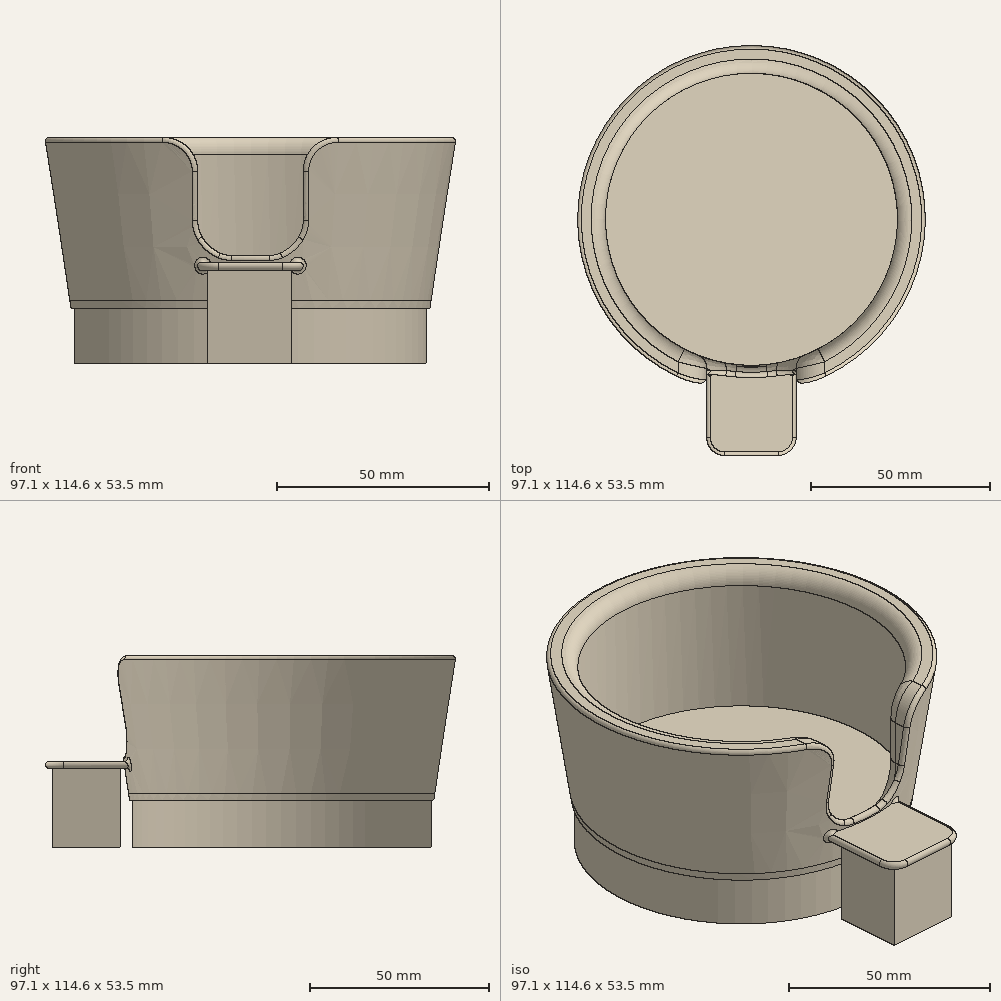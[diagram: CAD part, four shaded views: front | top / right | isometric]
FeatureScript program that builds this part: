
annotation { "Feature Type Name" : "Feature", "Feature Type Description" : "" }
export const myFeature = defineFeature(function(context is Context, id is Id, definition is map)
    precondition{}
    {
        {
            var Q0;
            Q0=qCreatedBy(makeId("Top.planeOp"),FACE);
            var sketch = newSketch(context, id + "F0", { "sketchPlane" : qUnion([Q0])});
            skCircle(sketch, "E0", {"center": v(0, 0) * mm, "radius": 34.5 * mm});
            skSolve(sketch);
        }
        {
            var Q0;
            Q0=qSketchRegion(id+"F0",true);
            extrude(context, id + "F1", {"entities" : qUnion([Q0]), "depth" : 13 * mm, "offsetDistance" : 25 * mm, "hasDraft" : true, "draftAngle" : 8.75 * degree});
        }
        {
            var Q0;
            Q0=makeQuery(id+"F1.opExtrude","CAP_FACE",FACE,{"disambiguationData":[OSD([sQuery(id+"F0.wireOp",EDGE,"E0")])],"isStart":false});
            var sketch = newSketch(context, id + "F2", { "sketchPlane" : qUnion([Q0])});
            skCircle(sketch, "E1", {"center": v(0, 0) * mm, "radius": 42.5 * mm});
            skSolve(sketch);
        }
        {
            var Q0;
            Q0=qSketchRegion(id+"F2",true);
            extrude(context, id + "F3", {"entities" : qUnion([Q0]), "operationType" : NewBodyOperationType.ADD, "depth" : 2 * mm, "offsetDistance" : 25 * mm, "hasDraft" : true, "draftAngle" : 8.7 * degree});
        }
        {
            var Q0;
            Q0=qCreatedBy(makeId("Right.planeOp"),FACE);
            var sketch = newSketch(context, id + "F4", { "sketchPlane" : qUnion([Q0])});
            skPoint(sketch, "E2", {"position": v(0, 15) * mm});
            skPoint(sketch, "E3", {"position": v(-42.8, 15) * mm});
            skPoint(sketch, "E4", {"position": v(-40.8, 15) * mm});
            skLineSegment(sketch, "E5", {"start": v(-42.8, 15) * mm, "end": v(-48.74, 53.55) * mm});
            skLineSegment(sketch, "E6", {"start": v(-42.8, 15) * mm, "end": v(-42.8, 65.75) * mm, "construction": true});
            skLineSegment(sketch, "E7", {"start": v(0, 15) * mm, "end": v(0, 72.45) * mm, "construction": true});
            skLineSegment(sketch, "E8", {"start": v(-40.8, 15) * mm, "end": v(-42.8, 15) * mm});
            skLineSegment(sketch, "E9", {"start": v(-46.74, 53.55) * mm, "end": v(-48.74, 53.55) * mm, "construction": true});
            skLineSegment(sketch, "E10", {"start": v(-40.8, 15) * mm, "end": v(-40.8, 53.55) * mm});
            skLineSegment(sketch, "E11", {"start": v(-48.74, 53.55) * mm, "end": v(-40.8, 53.55) * mm});
            skSolve(sketch);
        }
        {
            var Q0;
            Q0=qSketchRegion(id+"F4",true);
            var Q1;
            Q1=sQuery(id+"F4.wireOp",EDGE,"E7");
            revolve(context, id + "F5", {"operationType" : NewBodyOperationType.ADD, "surfaceOperationType" : NewSurfaceOperationType.NEW, "entities" : qUnion([Q0]), "axis" : qUnion([Q1]), "revolveType" : RevolveType.FULL});
        }
        {
            var Q0;
            Q0=qCreatedBy(makeId("Front.planeOp"),FACE);
            var sketch = newSketch(context, id + "F6", { "sketchPlane" : qUnion([Q0])});
            skPoint(sketch, "E12", {"position": v(0, 13) * mm});
            skPoint(sketch, "E13", {"position": v(0, 26) * mm});
            skPoint(sketch, "E14", {"position": v(0, 66) * mm});
            skPoint(sketch, "E15", {"position": v(-12.5, 66) * mm});
            skPoint(sketch, "E16", {"position": v(12.5, 66) * mm});
            skLineSegment(sketch, "E17.bottom", {"start": v(-12.5, 66) * mm, "end": v(12.5, 66) * mm});
            skLineSegment(sketch, "E17.top", {"start": v(-12.5, 26) * mm, "end": v(12.5, 26) * mm});
            skLineSegment(sketch, "E17.left", {"start": v(-12.5, 66) * mm, "end": v(-12.5, 26) * mm});
            skLineSegment(sketch, "E17.right", {"start": v(12.5, 66) * mm, "end": v(12.5, 26) * mm});
            skSolve(sketch);
        }
        {
            var Q0;
            Q0 = qSketchRegion(id + "F6", true);
            extrude(context, id + "F7", {"entities" : qUnion([Q0]), "operationType" : NewBodyOperationType.REMOVE, "endBound" : BoundingType.THROUGH_ALL, "depth" : 25 * mm, "offsetDistance" : 25 * mm});
        }
        {
            var Q0;
            Q0=makeQuery(id+"F7.boolean.opBoolean","COPY",EDGE,{"disambiguationData":[OD(0.0)],"derivedFrom":makeQuery(id+"F7.opExtrude","SWEPT_EDGE",EDGE,{"disambiguationData":[OSD([sQuery(id+"F6.wireOp",EDGE,"E17.top"),sQuery(id+"F6.wireOp",EDGE,"E17.left")])]})});
            var Q1;
            Q1=makeQuery(id+"F7.boolean.opBoolean","INTERSECT",EDGE,{"disambiguationData":[OD(0.0)],"derivedFrom":[makeQuery(id+"F5.opRevolve","SWEPT_FACE",FACE,{"disambiguationData":[OSD([sQuery(id+"F4.wireOp",EDGE,"E11")])]}),makeQuery(id+"F7.opExtrude","SWEPT_FACE",FACE,{"disambiguationData":[OSD([sQuery(id+"F6.wireOp",EDGE,"E17.left")])]})]});
            var Q2;
            Q2=makeQuery(id+"F7.boolean.opBoolean","INTERSECT",EDGE,{"disambiguationData":[OD(0.0)],"derivedFrom":[makeQuery(id+"F5.opRevolve","SWEPT_FACE",FACE,{"disambiguationData":[OSD([sQuery(id+"F4.wireOp",EDGE,"E11")])]}),makeQuery(id+"F7.opExtrude","SWEPT_FACE",FACE,{"disambiguationData":[OSD([sQuery(id+"F6.wireOp",EDGE,"E17.right")])]})]});
            var Q3;
            Q3=makeQuery(id+"F7.boolean.opBoolean","COPY",EDGE,{"disambiguationData":[OD(0.0)],"derivedFrom":makeQuery(id+"F7.opExtrude","SWEPT_EDGE",EDGE,{"disambiguationData":[OSD([sQuery(id+"F6.wireOp",EDGE,"E17.top"),sQuery(id+"F6.wireOp",EDGE,"E17.right")])]})});
            var Q4;
            Q4=makeQuery(id+"F7.boolean.opBoolean","INTERSECT",EDGE,{"disambiguationData":[OD(1.0)],"derivedFrom":[makeQuery(id+"F5.opRevolve","SWEPT_FACE",FACE,{"disambiguationData":[OSD([sQuery(id+"F4.wireOp",EDGE,"E11")])]}),makeQuery(id+"F7.opExtrude","SWEPT_FACE",FACE,{"disambiguationData":[OSD([sQuery(id+"F6.wireOp",EDGE,"E17.right")])]})]});
            var Q5;
            Q5=makeQuery(id+"F7.boolean.opBoolean","INTERSECT",EDGE,{"disambiguationData":[OD(1.0)],"derivedFrom":[makeQuery(id+"F5.opRevolve","SWEPT_FACE",FACE,{"disambiguationData":[OSD([sQuery(id+"F4.wireOp",EDGE,"E11")])]}),makeQuery(id+"F7.opExtrude","SWEPT_FACE",FACE,{"disambiguationData":[OSD([sQuery(id+"F6.wireOp",EDGE,"E17.left")])]})]});
            var Q6;
            Q6=makeQuery(id+"F7.boolean.opBoolean","COPY",EDGE,{"disambiguationData":[OD(1.0)],"derivedFrom":makeQuery(id+"F7.opExtrude","SWEPT_EDGE",EDGE,{"disambiguationData":[OSD([sQuery(id+"F6.wireOp",EDGE,"E17.top"),sQuery(id+"F6.wireOp",EDGE,"E17.left")])]})});
            var Q7;
            Q7=makeQuery(id+"F7.boolean.opBoolean","COPY",EDGE,{"disambiguationData":[OD(1.0)],"derivedFrom":makeQuery(id+"F7.opExtrude","SWEPT_EDGE",EDGE,{"disambiguationData":[OSD([sQuery(id+"F6.wireOp",EDGE,"E17.top"),sQuery(id+"F6.wireOp",EDGE,"E17.right")])]})});
            fillet(context, id + "F8", {"entities" : qUnion([Q0, Q1, Q2, Q3, Q4, Q5, Q6, Q7]), "radius" : 8 * mm, "tangentPropagation" : true, "allowEdgeOverflow" : false});
        }
        {
            var Q0;
            {var subQ0=sQuery(id+"F4.wireOp",EDGE,"E10");var subQ1=sQuery(id+"F4.wireOp",EDGE,"E11");Q0=makeQuery(id+"F7.boolean.opBoolean","SPLIT",EDGE,{"disambiguationData":[TD([makeQuery(id+"F7.opExtrude","SWEPT_FACE",FACE,{"disambiguationData":[OSD([sQuery(id+"F6.wireOp",EDGE,"E17.right")])]})])],"derivedFrom":makeQuery(id+"F5.opRevolve","SWEPT_EDGE",EDGE,{"disambiguationData":[OSD([subQ0,subQ1])]})});}
            var Q1;
            {var subQ0=sQuery(id+"F4.wireOp",EDGE,"E10");var subQ1=sQuery(id+"F4.wireOp",EDGE,"E11");Q1=makeQuery(id+"F7.boolean.opBoolean","SPLIT",EDGE,{"disambiguationData":[TD([makeQuery(id+"F7.opExtrude","SWEPT_FACE",FACE,{"disambiguationData":[OSD([sQuery(id+"F6.wireOp",EDGE,"E17.left")])]})])],"derivedFrom":makeQuery(id+"F5.opRevolve","SWEPT_EDGE",EDGE,{"disambiguationData":[OSD([subQ0,subQ1])]})});}
            fillet(context, id + "F9", {"entities" : qUnion([Q0, Q1]), "radius" : 4 * mm, "tangentPropagation" : true, "allowEdgeOverflow" : false});
        }
        {
            var Q0;
            {var subQ0=sQuery(id+"F4.wireOp",EDGE,"E5");var subQ1=sQuery(id+"F4.wireOp",EDGE,"E11");Q0=makeQuery(id+"F7.boolean.opBoolean","SPLIT",EDGE,{"disambiguationData":[TD([makeQuery(id+"F7.opExtrude","SWEPT_FACE",FACE,{"disambiguationData":[OSD([sQuery(id+"F6.wireOp",EDGE,"E17.right")])]})])],"derivedFrom":makeQuery(id+"F5.opRevolve","SWEPT_EDGE",EDGE,{"disambiguationData":[OSD([subQ0,subQ1])]})});}
            var Q1;
            {var subQ0=sQuery(id+"F4.wireOp",EDGE,"E5");var subQ1=sQuery(id+"F4.wireOp",EDGE,"E11");Q1=makeQuery(id+"F7.boolean.opBoolean","SPLIT",EDGE,{"disambiguationData":[TD([makeQuery(id+"F7.opExtrude","SWEPT_FACE",FACE,{"disambiguationData":[OSD([sQuery(id+"F6.wireOp",EDGE,"E17.left")])]})])],"derivedFrom":makeQuery(id+"F5.opRevolve","SWEPT_EDGE",EDGE,{"disambiguationData":[OSD([subQ0,subQ1])]})});}
            var Q2;
            Q2=makeQuery(id+"F8.opFillet","BLEND_EDGE",EDGE,{"blendedFrom":[makeQuery(id+"F7.boolean.opBoolean","INTERSECT",EDGE,{"disambiguationData":[OD(1.0)],"derivedFrom":[makeQuery(id+"F5.opRevolve","SWEPT_FACE",FACE,{"disambiguationData":[OSD([sQuery(id+"F4.wireOp",EDGE,"E11")])]}),makeQuery(id+"F7.opExtrude","SWEPT_FACE",FACE,{"disambiguationData":[OSD([sQuery(id+"F6.wireOp",EDGE,"E17.right")])]})]}),makeQuery(id+"F5.opRevolve","SWEPT_FACE",FACE,{"disambiguationData":[OSD([sQuery(id+"F4.wireOp",EDGE,"E5")])]})],"blendedInto":[makeQuery(id+"F5.opRevolve","SWEPT_FACE",FACE,{"disambiguationData":[OSD([sQuery(id+"F4.wireOp",EDGE,"E5")])]})]});
            var Q3;
            Q3=makeQuery(id+"F8.opFillet","BLEND_EDGE",EDGE,{"blendedFrom":[makeQuery(id+"F7.boolean.opBoolean","INTERSECT",EDGE,{"disambiguationData":[OD(1.0)],"derivedFrom":[makeQuery(id+"F5.opRevolve","SWEPT_FACE",FACE,{"disambiguationData":[OSD([sQuery(id+"F4.wireOp",EDGE,"E11")])]}),makeQuery(id+"F7.opExtrude","SWEPT_FACE",FACE,{"disambiguationData":[OSD([sQuery(id+"F6.wireOp",EDGE,"E17.left")])]})]}),makeQuery(id+"F5.opRevolve","SWEPT_FACE",FACE,{"disambiguationData":[OSD([sQuery(id+"F4.wireOp",EDGE,"E5")])]})],"blendedInto":[makeQuery(id+"F5.opRevolve","SWEPT_FACE",FACE,{"disambiguationData":[OSD([sQuery(id+"F4.wireOp",EDGE,"E5")])]})]});
            var Q4;
            Q4=makeQuery(id+"F7.boolean.opBoolean","INTERSECT",EDGE,{"disambiguationData":[OD(1.0)],"derivedFrom":[makeQuery(id+"F5.opRevolve","SWEPT_FACE",FACE,{"disambiguationData":[OSD([sQuery(id+"F4.wireOp",EDGE,"E5")])]}),makeQuery(id+"F7.opExtrude","SWEPT_FACE",FACE,{"disambiguationData":[OSD([sQuery(id+"F6.wireOp",EDGE,"E17.left")])]})]});
            var Q5;
            Q5=makeQuery(id+"F8.opFillet","BLEND_EDGE",EDGE,{"blendedFrom":[makeQuery(id+"F7.boolean.opBoolean","COPY",EDGE,{"disambiguationData":[OD(1.0)],"derivedFrom":makeQuery(id+"F7.opExtrude","SWEPT_EDGE",EDGE,{"disambiguationData":[OSD([sQuery(id+"F6.wireOp",EDGE,"E17.top"),sQuery(id+"F6.wireOp",EDGE,"E17.left")])]})}),makeQuery(id+"F5.opRevolve","SWEPT_FACE",FACE,{"disambiguationData":[OSD([sQuery(id+"F4.wireOp",EDGE,"E5")])]})],"blendedInto":[makeQuery(id+"F5.opRevolve","SWEPT_FACE",FACE,{"disambiguationData":[OSD([sQuery(id+"F4.wireOp",EDGE,"E5")])]})]});
            var Q6;
            Q6=makeQuery(id+"F9.opFillet","BLEND_EDGE",EDGE,{"disambiguationData":[OD(1.0)],"blendedFrom":[makeQuery(id+"F8.opFillet","BLEND_EDGE",EDGE,{"blendedFrom":[makeQuery(id+"F7.boolean.opBoolean","COPY",EDGE,{"disambiguationData":[OD(1.0)],"derivedFrom":makeQuery(id+"F7.opExtrude","SWEPT_EDGE",EDGE,{"disambiguationData":[OSD([sQuery(id+"F6.wireOp",EDGE,"E17.top"),sQuery(id+"F6.wireOp",EDGE,"E17.left")])]})}),makeQuery(id+"F5.opRevolve","SWEPT_FACE",FACE,{"disambiguationData":[OSD([sQuery(id+"F4.wireOp",EDGE,"E10")])]})],"blendedInto":[makeQuery(id+"F5.opRevolve","SWEPT_FACE",FACE,{"disambiguationData":[OSD([sQuery(id+"F4.wireOp",EDGE,"E10")])]})]}),makeQuery(id+"F5.opRevolve","SWEPT_FACE",FACE,{"disambiguationData":[OSD([sQuery(id+"F4.wireOp",EDGE,"E5")])]})],"blendedInto":[makeQuery(id+"F5.opRevolve","SWEPT_FACE",FACE,{"disambiguationData":[OSD([sQuery(id+"F4.wireOp",EDGE,"E5")])]})]});
            var Q7;
            Q7=makeQuery(id+"F9.opFillet","BLEND_EDGE",EDGE,{"disambiguationData":[OD(0.0)],"blendedFrom":[makeQuery(id+"F8.opFillet","BLEND_EDGE",EDGE,{"blendedFrom":[makeQuery(id+"F7.boolean.opBoolean","COPY",EDGE,{"disambiguationData":[OD(1.0)],"derivedFrom":makeQuery(id+"F7.opExtrude","SWEPT_EDGE",EDGE,{"disambiguationData":[OSD([sQuery(id+"F6.wireOp",EDGE,"E17.top"),sQuery(id+"F6.wireOp",EDGE,"E17.left")])]})}),makeQuery(id+"F5.opRevolve","SWEPT_FACE",FACE,{"disambiguationData":[OSD([sQuery(id+"F4.wireOp",EDGE,"E10")])]})],"blendedInto":[makeQuery(id+"F5.opRevolve","SWEPT_FACE",FACE,{"disambiguationData":[OSD([sQuery(id+"F4.wireOp",EDGE,"E10")])]})]}),makeQuery(id+"F5.opRevolve","SWEPT_FACE",FACE,{"disambiguationData":[OSD([sQuery(id+"F4.wireOp",EDGE,"E5")])]})],"blendedInto":[makeQuery(id+"F5.opRevolve","SWEPT_FACE",FACE,{"disambiguationData":[OSD([sQuery(id+"F4.wireOp",EDGE,"E5")])]})]});
            var Q8;
            Q8=makeQuery(id+"F9.opFillet","BLEND_EDGE",EDGE,{"blendedFrom":[makeQuery(id+"F8.opFillet","BLEND_EDGE",EDGE,{"blendedFrom":[makeQuery(id+"F7.boolean.opBoolean","COPY",EDGE,{"disambiguationData":[OD(1.0)],"derivedFrom":makeQuery(id+"F7.opExtrude","SWEPT_EDGE",EDGE,{"disambiguationData":[OSD([sQuery(id+"F6.wireOp",EDGE,"E17.top"),sQuery(id+"F6.wireOp",EDGE,"E17.right")])]})}),makeQuery(id+"F5.opRevolve","SWEPT_FACE",FACE,{"disambiguationData":[OSD([sQuery(id+"F4.wireOp",EDGE,"E10")])]})],"blendedInto":[makeQuery(id+"F5.opRevolve","SWEPT_FACE",FACE,{"disambiguationData":[OSD([sQuery(id+"F4.wireOp",EDGE,"E10")])]})]}),makeQuery(id+"F5.opRevolve","SWEPT_FACE",FACE,{"disambiguationData":[OSD([sQuery(id+"F4.wireOp",EDGE,"E5")])]})],"blendedInto":[makeQuery(id+"F5.opRevolve","SWEPT_FACE",FACE,{"disambiguationData":[OSD([sQuery(id+"F4.wireOp",EDGE,"E5")])]})]});
            var Q9;
            Q9=makeQuery(id+"F8.opFillet","BLEND_EDGE",EDGE,{"blendedFrom":[makeQuery(id+"F7.boolean.opBoolean","COPY",EDGE,{"disambiguationData":[OD(1.0)],"derivedFrom":makeQuery(id+"F7.opExtrude","SWEPT_EDGE",EDGE,{"disambiguationData":[OSD([sQuery(id+"F6.wireOp",EDGE,"E17.top"),sQuery(id+"F6.wireOp",EDGE,"E17.right")])]})}),makeQuery(id+"F5.opRevolve","SWEPT_FACE",FACE,{"disambiguationData":[OSD([sQuery(id+"F4.wireOp",EDGE,"E5")])]})],"blendedInto":[makeQuery(id+"F5.opRevolve","SWEPT_FACE",FACE,{"disambiguationData":[OSD([sQuery(id+"F4.wireOp",EDGE,"E5")])]})]});
            var Q10;
            Q10=makeQuery(id+"F7.boolean.opBoolean","INTERSECT",EDGE,{"disambiguationData":[OD(1.0)],"derivedFrom":[makeQuery(id+"F5.opRevolve","SWEPT_FACE",FACE,{"disambiguationData":[OSD([sQuery(id+"F4.wireOp",EDGE,"E5")])]}),makeQuery(id+"F7.opExtrude","SWEPT_FACE",FACE,{"disambiguationData":[OSD([sQuery(id+"F6.wireOp",EDGE,"E17.right")])]})]});
            var Q11;
            Q11=makeQuery(id+"F9.opFillet","BLEND_EDGE",EDGE,{"blendedFrom":[makeQuery(id+"F8.opFillet","BLEND_EDGE",EDGE,{"blendedFrom":[makeQuery(id+"F7.boolean.opBoolean","COPY",EDGE,{"disambiguationData":[OD(0.0)],"derivedFrom":makeQuery(id+"F7.opExtrude","SWEPT_EDGE",EDGE,{"disambiguationData":[OSD([sQuery(id+"F6.wireOp",EDGE,"E17.top"),sQuery(id+"F6.wireOp",EDGE,"E17.left")])]})}),makeQuery(id+"F5.opRevolve","SWEPT_FACE",FACE,{"disambiguationData":[OSD([sQuery(id+"F4.wireOp",EDGE,"E10")])]})],"blendedInto":[makeQuery(id+"F5.opRevolve","SWEPT_FACE",FACE,{"disambiguationData":[OSD([sQuery(id+"F4.wireOp",EDGE,"E10")])]})]}),makeQuery(id+"F5.opRevolve","SWEPT_FACE",FACE,{"disambiguationData":[OSD([sQuery(id+"F4.wireOp",EDGE,"E5")])]})],"blendedInto":[makeQuery(id+"F5.opRevolve","SWEPT_FACE",FACE,{"disambiguationData":[OSD([sQuery(id+"F4.wireOp",EDGE,"E5")])]})]});
            var Q12;
            Q12=makeQuery(id+"F9.opFillet","BLEND_EDGE",EDGE,{"disambiguationData":[OD(0.0)],"blendedFrom":[makeQuery(id+"F8.opFillet","BLEND_EDGE",EDGE,{"blendedFrom":[makeQuery(id+"F7.boolean.opBoolean","COPY",EDGE,{"disambiguationData":[OD(0.0)],"derivedFrom":makeQuery(id+"F7.opExtrude","SWEPT_EDGE",EDGE,{"disambiguationData":[OSD([sQuery(id+"F6.wireOp",EDGE,"E17.top"),sQuery(id+"F6.wireOp",EDGE,"E17.right")])]})}),makeQuery(id+"F5.opRevolve","SWEPT_FACE",FACE,{"disambiguationData":[OSD([sQuery(id+"F4.wireOp",EDGE,"E10")])]})],"blendedInto":[makeQuery(id+"F5.opRevolve","SWEPT_FACE",FACE,{"disambiguationData":[OSD([sQuery(id+"F4.wireOp",EDGE,"E10")])]})]}),makeQuery(id+"F5.opRevolve","SWEPT_FACE",FACE,{"disambiguationData":[OSD([sQuery(id+"F4.wireOp",EDGE,"E5")])]})],"blendedInto":[makeQuery(id+"F5.opRevolve","SWEPT_FACE",FACE,{"disambiguationData":[OSD([sQuery(id+"F4.wireOp",EDGE,"E5")])]})]});
            var Q13;
            Q13=makeQuery(id+"F9.opFillet","BLEND_EDGE",EDGE,{"disambiguationData":[OD(1.0)],"blendedFrom":[makeQuery(id+"F8.opFillet","BLEND_EDGE",EDGE,{"blendedFrom":[makeQuery(id+"F7.boolean.opBoolean","COPY",EDGE,{"disambiguationData":[OD(0.0)],"derivedFrom":makeQuery(id+"F7.opExtrude","SWEPT_EDGE",EDGE,{"disambiguationData":[OSD([sQuery(id+"F6.wireOp",EDGE,"E17.top"),sQuery(id+"F6.wireOp",EDGE,"E17.right")])]})}),makeQuery(id+"F5.opRevolve","SWEPT_FACE",FACE,{"disambiguationData":[OSD([sQuery(id+"F4.wireOp",EDGE,"E10")])]})],"blendedInto":[makeQuery(id+"F5.opRevolve","SWEPT_FACE",FACE,{"disambiguationData":[OSD([sQuery(id+"F4.wireOp",EDGE,"E10")])]})]}),makeQuery(id+"F5.opRevolve","SWEPT_FACE",FACE,{"disambiguationData":[OSD([sQuery(id+"F4.wireOp",EDGE,"E5")])]})],"blendedInto":[makeQuery(id+"F5.opRevolve","SWEPT_FACE",FACE,{"disambiguationData":[OSD([sQuery(id+"F4.wireOp",EDGE,"E5")])]})]});
            var Q14;
            Q14=makeQuery(id+"F8.opFillet","BLEND_EDGE",EDGE,{"blendedFrom":[makeQuery(id+"F7.boolean.opBoolean","COPY",EDGE,{"disambiguationData":[OD(0.0)],"derivedFrom":makeQuery(id+"F7.opExtrude","SWEPT_EDGE",EDGE,{"disambiguationData":[OSD([sQuery(id+"F6.wireOp",EDGE,"E17.top"),sQuery(id+"F6.wireOp",EDGE,"E17.right")])]})}),makeQuery(id+"F5.opRevolve","SWEPT_FACE",FACE,{"disambiguationData":[OSD([sQuery(id+"F4.wireOp",EDGE,"E5")])]})],"blendedInto":[makeQuery(id+"F5.opRevolve","SWEPT_FACE",FACE,{"disambiguationData":[OSD([sQuery(id+"F4.wireOp",EDGE,"E5")])]})]});
            var Q15;
            Q15=makeQuery(id+"F7.boolean.opBoolean","INTERSECT",EDGE,{"disambiguationData":[OD(0.0)],"derivedFrom":[makeQuery(id+"F5.opRevolve","SWEPT_FACE",FACE,{"disambiguationData":[OSD([sQuery(id+"F4.wireOp",EDGE,"E5")])]}),makeQuery(id+"F7.opExtrude","SWEPT_FACE",FACE,{"disambiguationData":[OSD([sQuery(id+"F6.wireOp",EDGE,"E17.right")])]})]});
            var Q16;
            Q16=makeQuery(id+"F8.opFillet","BLEND_EDGE",EDGE,{"blendedFrom":[makeQuery(id+"F7.boolean.opBoolean","INTERSECT",EDGE,{"disambiguationData":[OD(0.0)],"derivedFrom":[makeQuery(id+"F5.opRevolve","SWEPT_FACE",FACE,{"disambiguationData":[OSD([sQuery(id+"F4.wireOp",EDGE,"E11")])]}),makeQuery(id+"F7.opExtrude","SWEPT_FACE",FACE,{"disambiguationData":[OSD([sQuery(id+"F6.wireOp",EDGE,"E17.right")])]})]}),makeQuery(id+"F5.opRevolve","SWEPT_FACE",FACE,{"disambiguationData":[OSD([sQuery(id+"F4.wireOp",EDGE,"E5")])]})],"blendedInto":[makeQuery(id+"F5.opRevolve","SWEPT_FACE",FACE,{"disambiguationData":[OSD([sQuery(id+"F4.wireOp",EDGE,"E5")])]})]});
            var Q17;
            Q17=makeQuery(id+"F8.opFillet","BLEND_EDGE",EDGE,{"blendedFrom":[makeQuery(id+"F7.boolean.opBoolean","COPY",EDGE,{"disambiguationData":[OD(0.0)],"derivedFrom":makeQuery(id+"F7.opExtrude","SWEPT_EDGE",EDGE,{"disambiguationData":[OSD([sQuery(id+"F6.wireOp",EDGE,"E17.top"),sQuery(id+"F6.wireOp",EDGE,"E17.left")])]})}),makeQuery(id+"F5.opRevolve","SWEPT_FACE",FACE,{"disambiguationData":[OSD([sQuery(id+"F4.wireOp",EDGE,"E5")])]})],"blendedInto":[makeQuery(id+"F5.opRevolve","SWEPT_FACE",FACE,{"disambiguationData":[OSD([sQuery(id+"F4.wireOp",EDGE,"E5")])]})]});
            var Q18;
            Q18=makeQuery(id+"F7.boolean.opBoolean","INTERSECT",EDGE,{"disambiguationData":[OD(0.0)],"derivedFrom":[makeQuery(id+"F5.opRevolve","SWEPT_FACE",FACE,{"disambiguationData":[OSD([sQuery(id+"F4.wireOp",EDGE,"E5")])]}),makeQuery(id+"F7.opExtrude","SWEPT_FACE",FACE,{"disambiguationData":[OSD([sQuery(id+"F6.wireOp",EDGE,"E17.left")])]})]});
            var Q19;
            Q19=makeQuery(id+"F8.opFillet","BLEND_EDGE",EDGE,{"blendedFrom":[makeQuery(id+"F7.boolean.opBoolean","INTERSECT",EDGE,{"disambiguationData":[OD(0.0)],"derivedFrom":[makeQuery(id+"F5.opRevolve","SWEPT_FACE",FACE,{"disambiguationData":[OSD([sQuery(id+"F4.wireOp",EDGE,"E11")])]}),makeQuery(id+"F7.opExtrude","SWEPT_FACE",FACE,{"disambiguationData":[OSD([sQuery(id+"F6.wireOp",EDGE,"E17.left")])]})]}),makeQuery(id+"F5.opRevolve","SWEPT_FACE",FACE,{"disambiguationData":[OSD([sQuery(id+"F4.wireOp",EDGE,"E5")])]})],"blendedInto":[makeQuery(id+"F5.opRevolve","SWEPT_FACE",FACE,{"disambiguationData":[OSD([sQuery(id+"F4.wireOp",EDGE,"E5")])]})]});
            fillet(context, id + "F10", {"entities" : qUnion([Q0, Q1, Q2, Q3, Q4, Q5, Q6, Q7, Q8, Q9, Q10, Q11, Q12, Q13, Q14, Q15, Q16, Q17, Q18, Q19]), "radius" : 1 * mm, "tangentPropagation" : true, "allowEdgeOverflow" : false});
        }
        {
            var Q0;
            Q0=qCreatedBy(makeId("Front.planeOp"),FACE);
            cPlane(context, id + "F11", {"entities" : qUnion([Q0]), "cplaneType" : CPlaneType.OFFSET, "offset" : 41 * mm, "width" : 150 * mm, "height" : 150 * mm});
        }
        {
            var Q0;
            Q0=qCreatedBy(id+"F11.planeOp",FACE);
            var sketch = newSketch(context, id + "F12", { "sketchPlane" : qUnion([Q0])});
            skPoint(sketch, "E18", {"position": v(0, 23) * mm});
            skLineSegment(sketch, "E19.bottom", {"start": v(12.5, 22) * mm, "end": v(-12.5, 22) * mm});
            skLineSegment(sketch, "E19.top", {"start": v(12.5, 24) * mm, "end": v(-12.5, 24) * mm});
            skLineSegment(sketch, "E19.left", {"start": v(12.5, 22) * mm, "end": v(12.5, 24) * mm});
            skLineSegment(sketch, "E19.right", {"start": v(-12.5, 22) * mm, "end": v(-12.5, 24) * mm});
            skSolve(sketch);
        }
        {
            var Q0;
            Q0 = qSketchRegion(id + "F12", true);
            extrude(context, id + "F13", {"entities" : qUnion([Q0]), "operationType" : NewBodyOperationType.ADD, "depth" : 25 * mm, "offsetDistance" : 25 * mm});
        }
        {
            var Q0;
            Q0=makeQuery(id+"F13.opExtrude","CAP_EDGE",EDGE,{"disambiguationData":[OSD([sQuery(id+"F12.wireOp",EDGE,"E19.left")])],"isStart":false});
            var Q1;
            Q1=makeQuery(id+"F13.opExtrude","CAP_EDGE",EDGE,{"disambiguationData":[OSD([sQuery(id+"F12.wireOp",EDGE,"E19.right")])],"isStart":false});
            fillet(context, id + "F14", {"entities" : qUnion([Q0, Q1]), "radius" : 5 * mm, "tangentPropagation" : true, "allowEdgeOverflow" : false});
        }
        {
            var Q0;
            Q0=makeQuery(id+"F13.opExtrude","SWEPT_FACE",FACE,{"disambiguationData":[OSD([sQuery(id+"F12.wireOp",EDGE,"E19.right")])]});
            var Q1;
            Q1=makeQuery(id+"F14.opFillet","BLEND_FACE",FACE,{"disambiguationData":[OSD([sQuery(id+"F12.wireOp",EDGE,"E19.right")])]});
            var Q2;
            Q2=makeQuery(id+"F13.opExtrude","CAP_FACE",FACE,{"disambiguationData":[OSD([sQuery(id+"F12.wireOp",EDGE,"E19.bottom"),sQuery(id+"F12.wireOp",EDGE,"E19.top"),sQuery(id+"F12.wireOp",EDGE,"E19.left"),sQuery(id+"F12.wireOp",EDGE,"E19.right")])],"isStart":false});
            var Q3;
            Q3=makeQuery(id+"F14.opFillet","BLEND_FACE",FACE,{"disambiguationData":[OSD([sQuery(id+"F12.wireOp",EDGE,"E19.left")])]});
            var Q4;
            Q4=makeQuery(id+"F13.opExtrude","SWEPT_FACE",FACE,{"disambiguationData":[OSD([sQuery(id+"F12.wireOp",EDGE,"E19.left")])]});
            fillet(context, id + "F15", {"entities" : qUnion([Q0, Q1, Q2, Q3, Q4]), "radius" : 1 * mm, "tangentPropagation" : true, "allowEdgeOverflow" : false});
        }
        {
            var Q0;
            Q0=makeQuery(id+"F3.opExtrude","CAP_FACE",FACE,{"disambiguationData":[OSD([sQuery(id+"F2.wireOp",EDGE,"E1")])],"isStart":true});
            var sketch = newSketch(context, id + "F16", { "sketchPlane" : qUnion([Q0])});
            skPoint(sketch, "E20", {"position": v(0, 0) * mm});
            skLineSegment(sketch, "E21.bottom", {"start": v(-37.6, 0) * mm, "end": v(-41.75, 0) * mm});
            skLineSegment(sketch, "E21.top", {"start": v(-37.6, 0.6) * mm, "end": v(-41.75, 0.6) * mm});
            skLineSegment(sketch, "E21.left", {"start": v(-37.6, 0) * mm, "end": v(-37.6, 0.6) * mm});
            skLineSegment(sketch, "E21.right", {"start": v(-41.75, 0) * mm, "end": v(-41.75, 0.6) * mm});
            skLineSegment(sketch, "E22.1.0", {"start": v(-35.76, -11.62) * mm, "end": v(-39.7, -12.9) * mm});
            skLineSegment(sketch, "E22.1.1", {"start": v(-35.95, -11.04) * mm, "end": v(-39.9, -12.33) * mm});
            skLineSegment(sketch, "E22.1.2", {"start": v(-35.76, -11.62) * mm, "end": v(-35.95, -11.04) * mm});
            skLineSegment(sketch, "E22.1.3", {"start": v(-39.7, -12.9) * mm, "end": v(-39.9, -12.33) * mm});
            skLineSegment(sketch, "E22.2.0", {"start": v(-30.42, -22.1) * mm, "end": v(-33.78, -24.54) * mm});
            skLineSegment(sketch, "E22.2.1", {"start": v(-30.77, -21.61) * mm, "end": v(-34.13, -24.05) * mm});
            skLineSegment(sketch, "E22.2.2", {"start": v(-30.42, -22.1) * mm, "end": v(-30.77, -21.61) * mm});
            skLineSegment(sketch, "E22.2.3", {"start": v(-33.78, -24.54) * mm, "end": v(-34.13, -24.05) * mm});
            skLineSegment(sketch, "E22.3.0", {"start": v(-22.1, -30.42) * mm, "end": v(-24.54, -33.78) * mm});
            skLineSegment(sketch, "E22.3.1", {"start": v(-22.59, -30.06) * mm, "end": v(-25.03, -33.42) * mm});
            skLineSegment(sketch, "E22.3.2", {"start": v(-22.1, -30.42) * mm, "end": v(-22.59, -30.06) * mm});
            skLineSegment(sketch, "E22.3.3", {"start": v(-24.54, -33.78) * mm, "end": v(-25.03, -33.42) * mm});
            skLineSegment(sketch, "E22.4.0", {"start": v(-11.62, -35.76) * mm, "end": v(-12.9, -39.7) * mm});
            skLineSegment(sketch, "E22.4.1", {"start": v(-12.2, -35.57) * mm, "end": v(-13.48, -39.52) * mm});
            skLineSegment(sketch, "E22.4.2", {"start": v(-11.62, -35.76) * mm, "end": v(-12.2, -35.57) * mm});
            skLineSegment(sketch, "E22.4.3", {"start": v(-12.9, -39.7) * mm, "end": v(-13.48, -39.52) * mm});
            skLineSegment(sketch, "E22.5.0", {"start": v(0, -37.6) * mm, "end": v(0, -41.75) * mm});
            skLineSegment(sketch, "E22.5.1", {"start": v(-0.6, -37.6) * mm, "end": v(-0.6, -41.75) * mm});
            skLineSegment(sketch, "E22.5.2", {"start": v(0, -37.6) * mm, "end": v(-0.6, -37.6) * mm});
            skLineSegment(sketch, "E22.5.3", {"start": v(0, -41.75) * mm, "end": v(-0.6, -41.75) * mm});
            skLineSegment(sketch, "E22.6.0", {"start": v(11.62, -35.76) * mm, "end": v(12.9, -39.7) * mm});
            skLineSegment(sketch, "E22.6.1", {"start": v(11.04, -35.95) * mm, "end": v(12.33, -39.9) * mm});
            skLineSegment(sketch, "E22.6.2", {"start": v(11.62, -35.76) * mm, "end": v(11.04, -35.95) * mm});
            skLineSegment(sketch, "E22.6.3", {"start": v(12.9, -39.7) * mm, "end": v(12.33, -39.9) * mm});
            skLineSegment(sketch, "E22.7.0", {"start": v(22.1, -30.42) * mm, "end": v(24.54, -33.78) * mm});
            skLineSegment(sketch, "E22.7.1", {"start": v(21.61, -30.77) * mm, "end": v(24.05, -34.13) * mm});
            skLineSegment(sketch, "E22.7.2", {"start": v(22.1, -30.42) * mm, "end": v(21.61, -30.77) * mm});
            skLineSegment(sketch, "E22.7.3", {"start": v(24.54, -33.78) * mm, "end": v(24.05, -34.13) * mm});
            skLineSegment(sketch, "E22.8.0", {"start": v(30.42, -22.1) * mm, "end": v(33.78, -24.54) * mm});
            skLineSegment(sketch, "E22.8.1", {"start": v(30.06, -22.59) * mm, "end": v(33.42, -25.03) * mm});
            skLineSegment(sketch, "E22.8.2", {"start": v(30.42, -22.1) * mm, "end": v(30.06, -22.59) * mm});
            skLineSegment(sketch, "E22.8.3", {"start": v(33.78, -24.54) * mm, "end": v(33.42, -25.03) * mm});
            skLineSegment(sketch, "E22.9.0", {"start": v(35.76, -11.62) * mm, "end": v(39.7, -12.9) * mm});
            skLineSegment(sketch, "E22.9.1", {"start": v(35.57, -12.2) * mm, "end": v(39.52, -13.48) * mm});
            skLineSegment(sketch, "E22.9.2", {"start": v(35.76, -11.62) * mm, "end": v(35.57, -12.2) * mm});
            skLineSegment(sketch, "E22.9.3", {"start": v(39.7, -12.9) * mm, "end": v(39.52, -13.48) * mm});
            skLineSegment(sketch, "E22.10.0", {"start": v(37.6, 0) * mm, "end": v(41.75, 0) * mm});
            skLineSegment(sketch, "E22.10.1", {"start": v(37.6, -0.6) * mm, "end": v(41.75, -0.6) * mm});
            skLineSegment(sketch, "E22.10.2", {"start": v(37.6, 0) * mm, "end": v(37.6, -0.6) * mm});
            skLineSegment(sketch, "E22.10.3", {"start": v(41.75, 0) * mm, "end": v(41.75, -0.6) * mm});
            skLineSegment(sketch, "E22.11.0", {"start": v(35.76, 11.62) * mm, "end": v(39.7, 12.9) * mm});
            skLineSegment(sketch, "E22.11.1", {"start": v(35.95, 11.04) * mm, "end": v(39.9, 12.33) * mm});
            skLineSegment(sketch, "E22.11.2", {"start": v(35.76, 11.62) * mm, "end": v(35.95, 11.04) * mm});
            skLineSegment(sketch, "E22.11.3", {"start": v(39.7, 12.9) * mm, "end": v(39.9, 12.33) * mm});
            skLineSegment(sketch, "E22.12.0", {"start": v(30.42, 22.1) * mm, "end": v(33.78, 24.54) * mm});
            skLineSegment(sketch, "E22.12.1", {"start": v(30.77, 21.61) * mm, "end": v(34.13, 24.05) * mm});
            skLineSegment(sketch, "E22.12.2", {"start": v(30.42, 22.1) * mm, "end": v(30.77, 21.61) * mm});
            skLineSegment(sketch, "E22.12.3", {"start": v(33.78, 24.54) * mm, "end": v(34.13, 24.05) * mm});
            skLineSegment(sketch, "E22.13.0", {"start": v(22.1, 30.42) * mm, "end": v(24.54, 33.78) * mm});
            skLineSegment(sketch, "E22.13.1", {"start": v(22.59, 30.06) * mm, "end": v(25.03, 33.42) * mm});
            skLineSegment(sketch, "E22.13.2", {"start": v(22.1, 30.42) * mm, "end": v(22.59, 30.06) * mm});
            skLineSegment(sketch, "E22.13.3", {"start": v(24.54, 33.78) * mm, "end": v(25.03, 33.42) * mm});
            skLineSegment(sketch, "E22.14.0", {"start": v(11.62, 35.76) * mm, "end": v(12.9, 39.7) * mm});
            skLineSegment(sketch, "E22.14.1", {"start": v(12.2, 35.57) * mm, "end": v(13.48, 39.52) * mm});
            skLineSegment(sketch, "E22.14.2", {"start": v(11.62, 35.76) * mm, "end": v(12.2, 35.57) * mm});
            skLineSegment(sketch, "E22.14.3", {"start": v(12.9, 39.7) * mm, "end": v(13.48, 39.52) * mm});
            skLineSegment(sketch, "E22.15.0", {"start": v(0, 37.6) * mm, "end": v(0, 41.75) * mm});
            skLineSegment(sketch, "E22.15.1", {"start": v(0.6, 37.6) * mm, "end": v(0.6, 41.75) * mm});
            skLineSegment(sketch, "E22.15.2", {"start": v(0, 37.6) * mm, "end": v(0.6, 37.6) * mm});
            skLineSegment(sketch, "E22.15.3", {"start": v(0, 41.75) * mm, "end": v(0.6, 41.75) * mm});
            skLineSegment(sketch, "E22.16.0", {"start": v(-11.62, 35.76) * mm, "end": v(-12.9, 39.7) * mm});
            skLineSegment(sketch, "E22.16.1", {"start": v(-11.04, 35.95) * mm, "end": v(-12.33, 39.9) * mm});
            skLineSegment(sketch, "E22.16.2", {"start": v(-11.62, 35.76) * mm, "end": v(-11.04, 35.95) * mm});
            skLineSegment(sketch, "E22.16.3", {"start": v(-12.9, 39.7) * mm, "end": v(-12.33, 39.9) * mm});
            skLineSegment(sketch, "E22.17.0", {"start": v(-22.1, 30.42) * mm, "end": v(-24.54, 33.78) * mm});
            skLineSegment(sketch, "E22.17.1", {"start": v(-21.61, 30.77) * mm, "end": v(-24.05, 34.13) * mm});
            skLineSegment(sketch, "E22.17.2", {"start": v(-22.1, 30.42) * mm, "end": v(-21.61, 30.77) * mm});
            skLineSegment(sketch, "E22.17.3", {"start": v(-24.54, 33.78) * mm, "end": v(-24.05, 34.13) * mm});
            skLineSegment(sketch, "E22.18.0", {"start": v(-30.42, 22.1) * mm, "end": v(-33.78, 24.54) * mm});
            skLineSegment(sketch, "E22.18.1", {"start": v(-30.06, 22.59) * mm, "end": v(-33.42, 25.03) * mm});
            skLineSegment(sketch, "E22.18.2", {"start": v(-30.42, 22.1) * mm, "end": v(-30.06, 22.59) * mm});
            skLineSegment(sketch, "E22.18.3", {"start": v(-33.78, 24.54) * mm, "end": v(-33.42, 25.03) * mm});
            skLineSegment(sketch, "E22.19.0", {"start": v(-35.76, 11.62) * mm, "end": v(-39.7, 12.9) * mm});
            skLineSegment(sketch, "E22.19.1", {"start": v(-35.57, 12.2) * mm, "end": v(-39.52, 13.48) * mm});
            skLineSegment(sketch, "E22.19.2", {"start": v(-35.76, 11.62) * mm, "end": v(-35.57, 12.2) * mm});
            skLineSegment(sketch, "E22.19.3", {"start": v(-39.7, 12.9) * mm, "end": v(-39.52, 13.48) * mm});
            skCircle(sketch, "E23", {"center": v(0, 0) * mm, "radius": 41.75 * mm});
            skCircle(sketch, "E24", {"center": v(0, 0) * mm, "radius": 41.1 * mm});
            skSolve(sketch);
        }
        {
            var Q0;
            Q0=makeQuery(id+"F16.imprint","IMPRINT",FACE,{"disambiguationData":[TD([[makeQuery(id+"F16.imprint","IMPRINT",EDGE,{"derivedFrom":sQuery(id+"F16.wireOp",EDGE,"E21.bottom")}),-1.0]])]});
            var Q1;
            Q1=makeQuery(id+"F16.imprint","IMPRINT",FACE,{"disambiguationData":[TD([[makeQuery(id+"F16.imprint","IMPRINT",EDGE,{"derivedFrom":sQuery(id+"F16.wireOp",EDGE,"E22.1.0")}),-1.0]])]});
            var Q2;
            Q2=makeQuery(id+"F16.imprint","IMPRINT",FACE,{"disambiguationData":[TD([[makeQuery(id+"F16.imprint","IMPRINT",EDGE,{"derivedFrom":sQuery(id+"F16.wireOp",EDGE,"E22.2.0")}),-1.0]])]});
            var Q3;
            Q3=makeQuery(id+"F16.imprint","IMPRINT",FACE,{"disambiguationData":[TD([[makeQuery(id+"F16.imprint","IMPRINT",EDGE,{"derivedFrom":sQuery(id+"F16.wireOp",EDGE,"E22.19.0")}),-1.0]])]});
            var Q4;
            Q4=makeQuery(id+"F16.imprint","IMPRINT",FACE,{"disambiguationData":[TD([[makeQuery(id+"F16.imprint","IMPRINT",EDGE,{"derivedFrom":sQuery(id+"F16.wireOp",EDGE,"E22.18.0")}),-1.0]])]});
            var Q5;
            Q5=makeQuery(id+"F16.imprint","IMPRINT",FACE,{"disambiguationData":[TD([[makeQuery(id+"F16.imprint","IMPRINT",EDGE,{"derivedFrom":sQuery(id+"F16.wireOp",EDGE,"E22.17.0")}),-1.0]])]});
            var Q6;
            Q6=makeQuery(id+"F16.imprint","IMPRINT",FACE,{"disambiguationData":[TD([[makeQuery(id+"F16.imprint","IMPRINT",EDGE,{"derivedFrom":sQuery(id+"F16.wireOp",EDGE,"E22.16.0")}),-1.0]])]});
            var Q7;
            Q7=makeQuery(id+"F16.imprint","IMPRINT",FACE,{"disambiguationData":[TD([[makeQuery(id+"F16.imprint","IMPRINT",EDGE,{"derivedFrom":sQuery(id+"F16.wireOp",EDGE,"E22.15.0")}),-1.0]])]});
            var Q8;
            Q8=makeQuery(id+"F16.imprint","IMPRINT",FACE,{"disambiguationData":[TD([[makeQuery(id+"F16.imprint","IMPRINT",EDGE,{"derivedFrom":sQuery(id+"F16.wireOp",EDGE,"E22.14.0")}),-1.0]])]});
            var Q9;
            Q9=makeQuery(id+"F16.imprint","IMPRINT",FACE,{"disambiguationData":[TD([[makeQuery(id+"F16.imprint","IMPRINT",EDGE,{"derivedFrom":sQuery(id+"F16.wireOp",EDGE,"E22.13.0")}),-1.0]])]});
            var Q10;
            Q10=makeQuery(id+"F16.imprint","IMPRINT",FACE,{"disambiguationData":[TD([[makeQuery(id+"F16.imprint","IMPRINT",EDGE,{"derivedFrom":sQuery(id+"F16.wireOp",EDGE,"E22.12.0")}),-1.0]])]});
            var Q11;
            Q11=makeQuery(id+"F16.imprint","IMPRINT",FACE,{"disambiguationData":[TD([[makeQuery(id+"F16.imprint","IMPRINT",EDGE,{"derivedFrom":sQuery(id+"F16.wireOp",EDGE,"E22.11.0")}),-1.0]])]});
            var Q12;
            Q12=makeQuery(id+"F16.imprint","IMPRINT",FACE,{"disambiguationData":[TD([[makeQuery(id+"F16.imprint","IMPRINT",EDGE,{"derivedFrom":sQuery(id+"F16.wireOp",EDGE,"E22.10.0")}),-1.0]])]});
            var Q13;
            Q13=makeQuery(id+"F16.imprint","IMPRINT",FACE,{"disambiguationData":[TD([[makeQuery(id+"F16.imprint","IMPRINT",EDGE,{"derivedFrom":sQuery(id+"F16.wireOp",EDGE,"E22.9.0")}),-1.0]])]});
            var Q14;
            Q14=makeQuery(id+"F16.imprint","IMPRINT",FACE,{"disambiguationData":[TD([[makeQuery(id+"F16.imprint","IMPRINT",EDGE,{"derivedFrom":sQuery(id+"F16.wireOp",EDGE,"E22.8.0")}),-1.0]])]});
            var Q15;
            Q15=makeQuery(id+"F16.imprint","IMPRINT",FACE,{"disambiguationData":[TD([[makeQuery(id+"F16.imprint","IMPRINT",EDGE,{"derivedFrom":sQuery(id+"F16.wireOp",EDGE,"E22.7.0")}),-1.0]])]});
            var Q16;
            Q16=makeQuery(id+"F16.imprint","IMPRINT",FACE,{"disambiguationData":[TD([[makeQuery(id+"F16.imprint","IMPRINT",EDGE,{"derivedFrom":sQuery(id+"F16.wireOp",EDGE,"E22.6.0")}),-1.0]])]});
            var Q17;
            Q17=makeQuery(id+"F16.imprint","IMPRINT",FACE,{"disambiguationData":[TD([[makeQuery(id+"F16.imprint","IMPRINT",EDGE,{"derivedFrom":sQuery(id+"F16.wireOp",EDGE,"E22.3.0")}),-1.0]])]});
            var Q18;
            Q18=makeQuery(id+"F16.imprint","IMPRINT",FACE,{"disambiguationData":[TD([[makeQuery(id+"F16.imprint","IMPRINT",EDGE,{"derivedFrom":sQuery(id+"F16.wireOp",EDGE,"E22.4.0")}),-1.0]])]});
            var Q19;
            Q19=makeQuery(id+"F16.imprint","IMPRINT",FACE,{"disambiguationData":[TD([[makeQuery(id+"F16.imprint","IMPRINT",EDGE,{"derivedFrom":sQuery(id+"F16.wireOp",EDGE,"E22.5.0")}),-1.0]])]});
            var Q20;
            {var subQ3=sQuery(id+"F16.wireOp",EDGE,"E24");var subQ5=sQuery(id+"F16.wireOp",EDGE,"E22.11.1");var subQ6=makeQuery(id+"F16.imprint","INTERSECT",VERTEX,{"derivedFrom":[subQ5,subQ3]});Q20=makeQuery(id+"F16.imprint","IMPRINT",FACE,{"disambiguationData":[TD([[makeQuery(id+"F16.imprint","IMPRINT",EDGE,{"disambiguationData":[TD([[subQ6,-1.0]])],"derivedFrom":subQ5}),-1.0]])]});}
            var Q21;
            {var subQ3=sQuery(id+"F16.wireOp",EDGE,"E24");var subQ5=sQuery(id+"F16.wireOp",EDGE,"E22.10.1");var subQ6=makeQuery(id+"F16.imprint","INTERSECT",VERTEX,{"derivedFrom":[subQ5,subQ3]});Q21=makeQuery(id+"F16.imprint","IMPRINT",FACE,{"disambiguationData":[TD([[makeQuery(id+"F16.imprint","IMPRINT",EDGE,{"disambiguationData":[TD([[subQ6,-1.0]])],"derivedFrom":subQ5}),-1.0]])]});}
            var Q22;
            {var subQ3=sQuery(id+"F16.wireOp",EDGE,"E24");var subQ5=sQuery(id+"F16.wireOp",EDGE,"E22.9.1");var subQ6=makeQuery(id+"F16.imprint","INTERSECT",VERTEX,{"derivedFrom":[subQ5,subQ3]});Q22=makeQuery(id+"F16.imprint","IMPRINT",FACE,{"disambiguationData":[TD([[makeQuery(id+"F16.imprint","IMPRINT",EDGE,{"disambiguationData":[TD([[subQ6,-1.0]])],"derivedFrom":subQ5}),-1.0]])]});}
            var Q23;
            {var subQ3=sQuery(id+"F16.wireOp",EDGE,"E24");var subQ5=sQuery(id+"F16.wireOp",EDGE,"E22.8.1");var subQ6=makeQuery(id+"F16.imprint","INTERSECT",VERTEX,{"derivedFrom":[subQ5,subQ3]});Q23=makeQuery(id+"F16.imprint","IMPRINT",FACE,{"disambiguationData":[TD([[makeQuery(id+"F16.imprint","IMPRINT",EDGE,{"disambiguationData":[TD([[subQ6,-1.0]])],"derivedFrom":subQ5}),-1.0]])]});}
            var Q24;
            {var subQ3=sQuery(id+"F16.wireOp",EDGE,"E24");var subQ5=sQuery(id+"F16.wireOp",EDGE,"E22.7.1");var subQ6=makeQuery(id+"F16.imprint","INTERSECT",VERTEX,{"derivedFrom":[subQ5,subQ3]});Q24=makeQuery(id+"F16.imprint","IMPRINT",FACE,{"disambiguationData":[TD([[makeQuery(id+"F16.imprint","IMPRINT",EDGE,{"disambiguationData":[TD([[subQ6,-1.0]])],"derivedFrom":subQ5}),-1.0]])]});}
            var Q25;
            {var subQ3=sQuery(id+"F16.wireOp",EDGE,"E24");var subQ5=sQuery(id+"F16.wireOp",EDGE,"E22.6.1");var subQ6=makeQuery(id+"F16.imprint","INTERSECT",VERTEX,{"derivedFrom":[subQ5,subQ3]});Q25=makeQuery(id+"F16.imprint","IMPRINT",FACE,{"disambiguationData":[TD([[makeQuery(id+"F16.imprint","IMPRINT",EDGE,{"disambiguationData":[TD([[subQ6,-1.0]])],"derivedFrom":subQ5}),-1.0]])]});}
            var Q26;
            {var subQ3=sQuery(id+"F16.wireOp",EDGE,"E24");var subQ5=sQuery(id+"F16.wireOp",EDGE,"E22.5.1");var subQ6=makeQuery(id+"F16.imprint","INTERSECT",VERTEX,{"derivedFrom":[subQ5,subQ3]});Q26=makeQuery(id+"F16.imprint","IMPRINT",FACE,{"disambiguationData":[TD([[makeQuery(id+"F16.imprint","IMPRINT",EDGE,{"disambiguationData":[TD([[subQ6,-1.0]])],"derivedFrom":subQ5}),-1.0]])]});}
            var Q27;
            {var subQ3=sQuery(id+"F16.wireOp",EDGE,"E24");var subQ5=sQuery(id+"F16.wireOp",EDGE,"E22.4.1");var subQ6=makeQuery(id+"F16.imprint","INTERSECT",VERTEX,{"derivedFrom":[subQ5,subQ3]});Q27=makeQuery(id+"F16.imprint","IMPRINT",FACE,{"disambiguationData":[TD([[makeQuery(id+"F16.imprint","IMPRINT",EDGE,{"disambiguationData":[TD([[subQ6,-1.0]])],"derivedFrom":subQ5}),-1.0]])]});}
            var Q28;
            {var subQ3=sQuery(id+"F16.wireOp",EDGE,"E24");var subQ5=sQuery(id+"F16.wireOp",EDGE,"E22.12.1");var subQ6=makeQuery(id+"F16.imprint","INTERSECT",VERTEX,{"derivedFrom":[subQ5,subQ3]});Q28=makeQuery(id+"F16.imprint","IMPRINT",FACE,{"disambiguationData":[TD([[makeQuery(id+"F16.imprint","IMPRINT",EDGE,{"disambiguationData":[TD([[subQ6,-1.0]])],"derivedFrom":subQ5}),-1.0]])]});}
            var Q29;
            {var subQ3=sQuery(id+"F16.wireOp",EDGE,"E24");var subQ5=sQuery(id+"F16.wireOp",EDGE,"E22.13.1");var subQ6=makeQuery(id+"F16.imprint","INTERSECT",VERTEX,{"derivedFrom":[subQ5,subQ3]});Q29=makeQuery(id+"F16.imprint","IMPRINT",FACE,{"disambiguationData":[TD([[makeQuery(id+"F16.imprint","IMPRINT",EDGE,{"disambiguationData":[TD([[subQ6,-1.0]])],"derivedFrom":subQ5}),-1.0]])]});}
            var Q30;
            {var subQ3=sQuery(id+"F16.wireOp",EDGE,"E24");var subQ5=sQuery(id+"F16.wireOp",EDGE,"E22.14.1");var subQ6=makeQuery(id+"F16.imprint","INTERSECT",VERTEX,{"derivedFrom":[subQ5,subQ3]});Q30=makeQuery(id+"F16.imprint","IMPRINT",FACE,{"disambiguationData":[TD([[makeQuery(id+"F16.imprint","IMPRINT",EDGE,{"disambiguationData":[TD([[subQ6,-1.0]])],"derivedFrom":subQ5}),-1.0]])]});}
            var Q31;
            {var subQ3=sQuery(id+"F16.wireOp",EDGE,"E24");var subQ5=sQuery(id+"F16.wireOp",EDGE,"E22.15.1");var subQ6=makeQuery(id+"F16.imprint","INTERSECT",VERTEX,{"derivedFrom":[subQ5,subQ3]});Q31=makeQuery(id+"F16.imprint","IMPRINT",FACE,{"disambiguationData":[TD([[makeQuery(id+"F16.imprint","IMPRINT",EDGE,{"disambiguationData":[TD([[subQ6,-1.0]])],"derivedFrom":subQ5}),-1.0]])]});}
            var Q32;
            {var subQ3=sQuery(id+"F16.wireOp",EDGE,"E24");var subQ5=sQuery(id+"F16.wireOp",EDGE,"E22.16.1");var subQ6=makeQuery(id+"F16.imprint","INTERSECT",VERTEX,{"derivedFrom":[subQ5,subQ3]});Q32=makeQuery(id+"F16.imprint","IMPRINT",FACE,{"disambiguationData":[TD([[makeQuery(id+"F16.imprint","IMPRINT",EDGE,{"disambiguationData":[TD([[subQ6,-1.0]])],"derivedFrom":subQ5}),-1.0]])]});}
            var Q33;
            {var subQ3=sQuery(id+"F16.wireOp",EDGE,"E24");var subQ5=sQuery(id+"F16.wireOp",EDGE,"E22.17.1");var subQ6=makeQuery(id+"F16.imprint","INTERSECT",VERTEX,{"derivedFrom":[subQ5,subQ3]});Q33=makeQuery(id+"F16.imprint","IMPRINT",FACE,{"disambiguationData":[TD([[makeQuery(id+"F16.imprint","IMPRINT",EDGE,{"disambiguationData":[TD([[subQ6,-1.0]])],"derivedFrom":subQ5}),-1.0]])]});}
            var Q34;
            {var subQ3=sQuery(id+"F16.wireOp",EDGE,"E24");var subQ5=sQuery(id+"F16.wireOp",EDGE,"E22.18.1");var subQ6=makeQuery(id+"F16.imprint","INTERSECT",VERTEX,{"derivedFrom":[subQ5,subQ3]});Q34=makeQuery(id+"F16.imprint","IMPRINT",FACE,{"disambiguationData":[TD([[makeQuery(id+"F16.imprint","IMPRINT",EDGE,{"disambiguationData":[TD([[subQ6,-1.0]])],"derivedFrom":subQ5}),-1.0]])]});}
            var Q35;
            {var subQ3=sQuery(id+"F16.wireOp",EDGE,"E24");var subQ5=sQuery(id+"F16.wireOp",EDGE,"E22.19.1");var subQ6=makeQuery(id+"F16.imprint","INTERSECT",VERTEX,{"derivedFrom":[subQ5,subQ3]});Q35=makeQuery(id+"F16.imprint","IMPRINT",FACE,{"disambiguationData":[TD([[makeQuery(id+"F16.imprint","IMPRINT",EDGE,{"disambiguationData":[TD([[subQ6,-1.0]])],"derivedFrom":subQ5}),-1.0]])]});}
            var Q36;
            {var subQ0=sQuery(id+"F16.wireOp",EDGE,"E24");var subQ1=sQuery(id+"F16.wireOp",EDGE,"E21.top");var subQ2=makeQuery(id+"F16.imprint","INTERSECT",VERTEX,{"derivedFrom":[subQ1,subQ0]});Q36=makeQuery(id+"F16.imprint","IMPRINT",FACE,{"disambiguationData":[TD([[makeQuery(id+"F16.imprint","IMPRINT",EDGE,{"disambiguationData":[TD([[subQ2,-1.0]])],"derivedFrom":subQ1}),-1.0]])]});}
            var Q37;
            {var subQ3=sQuery(id+"F16.wireOp",EDGE,"E24");var subQ5=sQuery(id+"F16.wireOp",EDGE,"E22.1.1");var subQ6=makeQuery(id+"F16.imprint","INTERSECT",VERTEX,{"derivedFrom":[subQ5,subQ3]});Q37=makeQuery(id+"F16.imprint","IMPRINT",FACE,{"disambiguationData":[TD([[makeQuery(id+"F16.imprint","IMPRINT",EDGE,{"disambiguationData":[TD([[subQ6,-1.0]])],"derivedFrom":subQ5}),-1.0]])]});}
            var Q38;
            {var subQ3=sQuery(id+"F16.wireOp",EDGE,"E24");var subQ5=sQuery(id+"F16.wireOp",EDGE,"E22.2.1");var subQ6=makeQuery(id+"F16.imprint","INTERSECT",VERTEX,{"derivedFrom":[subQ5,subQ3]});Q38=makeQuery(id+"F16.imprint","IMPRINT",FACE,{"disambiguationData":[TD([[makeQuery(id+"F16.imprint","IMPRINT",EDGE,{"disambiguationData":[TD([[subQ6,-1.0]])],"derivedFrom":subQ5}),-1.0]])]});}
            var Q39;
            {var subQ3=sQuery(id+"F16.wireOp",EDGE,"E24");var subQ5=sQuery(id+"F16.wireOp",EDGE,"E22.3.1");var subQ6=makeQuery(id+"F16.imprint","INTERSECT",VERTEX,{"derivedFrom":[subQ5,subQ3]});Q39=makeQuery(id+"F16.imprint","IMPRINT",FACE,{"disambiguationData":[TD([[makeQuery(id+"F16.imprint","IMPRINT",EDGE,{"disambiguationData":[TD([[subQ6,-1.0]])],"derivedFrom":subQ5}),-1.0]])]});}
            var Q40;
            Q40=makeQuery(id+"F1.opExtrude","CAP_FACE",FACE,{"disambiguationData":[OSD([sQuery(id+"F0.wireOp",EDGE,"E0")])],"isStart":true});
            extrude(context, id + "F17", {"entities" : qUnion([Q0, Q1, Q2, Q3, Q4, Q5, Q6, Q7, Q8, Q9, Q10, Q11, Q12, Q13, Q14, Q15, Q16, Q17, Q18, Q19, Q20, Q21, Q22, Q23, Q24, Q25, Q26, Q27, Q28, Q29, Q30, Q31, Q32, Q33, Q34, Q35, Q36, Q37, Q38, Q39]), "operationType" : NewBodyOperationType.ADD, "endBound" : BoundingType.UP_TO_SURFACE, "depth" : 25 * mm, "endBoundEntityFace" : qUnion([Q40]), "offsetDistance" : 25 * mm});
        }
        {
            var Q0;
            Q0=makeQuery(id+"F13.opExtrude","SWEPT_FACE",FACE,{"disambiguationData":[OSD([sQuery(id+"F12.wireOp",EDGE,"E19.bottom")])]});
            var sketch = newSketch(context, id + "F18", { "sketchPlane" : qUnion([Q0])});
            skLineSegment(sketch, "E25.bottom", {"start": v(9.8, 45.16) * mm, "end": v(-10.2, 45.16) * mm});
            skLineSegment(sketch, "E25.top", {"start": v(9.8, 63.96) * mm, "end": v(-10.2, 63.96) * mm});
            skLineSegment(sketch, "E25.left", {"start": v(9.8, 45.16) * mm, "end": v(9.8, 63.96) * mm});
            skLineSegment(sketch, "E25.right", {"start": v(-10.2, 45.16) * mm, "end": v(-10.2, 63.96) * mm});
            skPoint(sketch, "E26", {"position": v(9.2, 45.76) * mm});
            skPoint(sketch, "E27", {"position": v(-9.6, 63.36) * mm});
            skLineSegment(sketch, "E28.bottom", {"start": v(9.2, 45.76) * mm, "end": v(-9.6, 45.76) * mm});
            skLineSegment(sketch, "E28.top", {"start": v(9.2, 63.36) * mm, "end": v(-9.6, 63.36) * mm});
            skLineSegment(sketch, "E28.left", {"start": v(9.2, 45.76) * mm, "end": v(9.2, 63.36) * mm});
            skLineSegment(sketch, "E28.right", {"start": v(-9.6, 45.76) * mm, "end": v(-9.6, 63.36) * mm});
            skPoint(sketch, "E29", {"position": v(4.2, 50.76) * mm});
            skPoint(sketch, "E30", {"position": v(-4.6, 58.36) * mm});
            skPoint(sketch, "E31", {"position": v(3.6, 51.36) * mm});
            skPoint(sketch, "E32", {"position": v(-4, 57.76) * mm});
            skLineSegment(sketch, "E33.bottom", {"start": v(4.2, 50.76) * mm, "end": v(-4.6, 50.76) * mm});
            skLineSegment(sketch, "E33.top", {"start": v(4.2, 58.36) * mm, "end": v(-4.6, 58.36) * mm});
            skLineSegment(sketch, "E33.left", {"start": v(4.2, 50.76) * mm, "end": v(4.2, 58.36) * mm});
            skLineSegment(sketch, "E33.right", {"start": v(-4.6, 50.76) * mm, "end": v(-4.6, 58.36) * mm});
            skLineSegment(sketch, "E34.bottom", {"start": v(3.6, 51.36) * mm, "end": v(-4, 51.36) * mm});
            skLineSegment(sketch, "E34.top", {"start": v(3.6, 57.76) * mm, "end": v(-4, 57.76) * mm});
            skLineSegment(sketch, "E34.left", {"start": v(3.6, 51.36) * mm, "end": v(3.6, 57.76) * mm});
            skLineSegment(sketch, "E34.right", {"start": v(-4, 51.36) * mm, "end": v(-4, 57.76) * mm});
            skLineSegment(sketch, "E35.bottom", {"start": v(0, 51.36) * mm, "end": v(-0.6, 51.36) * mm});
            skLineSegment(sketch, "E35.top", {"start": v(0, 57.76) * mm, "end": v(-0.6, 57.76) * mm});
            skLineSegment(sketch, "E35.left", {"start": v(0, 51.36) * mm, "end": v(0, 57.76) * mm});
            skLineSegment(sketch, "E35.right", {"start": v(-0.6, 51.36) * mm, "end": v(-0.6, 57.76) * mm});
            skSolve(sketch);
        }
        {
            var Q0;
            Q0 = qSketchRegion(id + "F18", true);
            var Q1;
            Q1=makeQuery(id+"F18.imprint","IMPRINT",FACE,{"disambiguationData":[TD([[makeQuery(id+"F18.imprint","IMPRINT",EDGE,{"derivedFrom":sQuery(id+"F18.wireOp",EDGE,"E33.bottom")}),-1.0]])]});
            var Q2;
            Q2=makeQuery(id+"F18.imprint","IMPRINT",FACE,{"disambiguationData":[TD([[makeQuery(id+"F18.imprint","IMPRINT",EDGE,{"derivedFrom":sQuery(id+"F18.wireOp",EDGE,"E35.bottom")}),-1.0]])]});
            var Q3;
            Q3=makeQuery(id+"F1.opExtrude","CAP_FACE",FACE,{"disambiguationData":[OSD([sQuery(id+"F0.wireOp",EDGE,"E0")])],"isStart":true});
            extrude(context, id + "F19", {"entities" : qUnion([Q0, Q1, Q2]), "operationType" : NewBodyOperationType.ADD, "endBound" : BoundingType.UP_TO_SURFACE, "depth" : 25 * mm, "endBoundEntityFace" : qUnion([Q3]), "offsetDistance" : 25 * mm});
        }
        {
            var Q0;
            Q0=makeQuery(id+"F19.opExtrude","CAP_FACE",FACE,{"disambiguationData":[OSD([sQuery(id+"F18.wireOp",EDGE,"E25.bottom"),sQuery(id+"F18.wireOp",EDGE,"E25.top"),sQuery(id+"F18.wireOp",EDGE,"E25.left"),sQuery(id+"F18.wireOp",EDGE,"E25.right"),sQuery(id+"F18.wireOp",EDGE,"E28.bottom"),sQuery(id+"F18.wireOp",EDGE,"E28.top"),sQuery(id+"F18.wireOp",EDGE,"E28.left"),sQuery(id+"F18.wireOp",EDGE,"E28.right")])],"isStart":false});
            var sketch = newSketch(context, id + "F20", { "sketchPlane" : qUnion([Q0])});
            skLineSegment(sketch, "E36.bottom", {"start": v(9.8, 63.96) * mm, "end": v(-10.2, 63.96) * mm});
            skLineSegment(sketch, "E36.top", {"start": v(9.8, 45.16) * mm, "end": v(-10.2, 45.16) * mm});
            skLineSegment(sketch, "E36.left", {"start": v(9.8, 63.96) * mm, "end": v(9.8, 45.16) * mm});
            skLineSegment(sketch, "E36.right", {"start": v(-10.2, 63.96) * mm, "end": v(-10.2, 45.16) * mm});
            skCircle(sketch, "E37", {"center": v(0, 0) * mm, "radius": 37.6 * mm});
            skCircle(sketch, "E38", {"center": v(0, 0) * mm, "radius": 41.75 * mm});
            skSolve(sketch);
        }
        {
            var Q0;
            Q0 = qSketchRegion(id + "F20", true);
            extrude(context, id + "F21", {"entities" : qUnion([Q0]), "operationType" : NewBodyOperationType.ADD, "oppositeDirection" : true, "depth" : 1 * mm, "offsetDistance" : 25 * mm});
        }
    });
